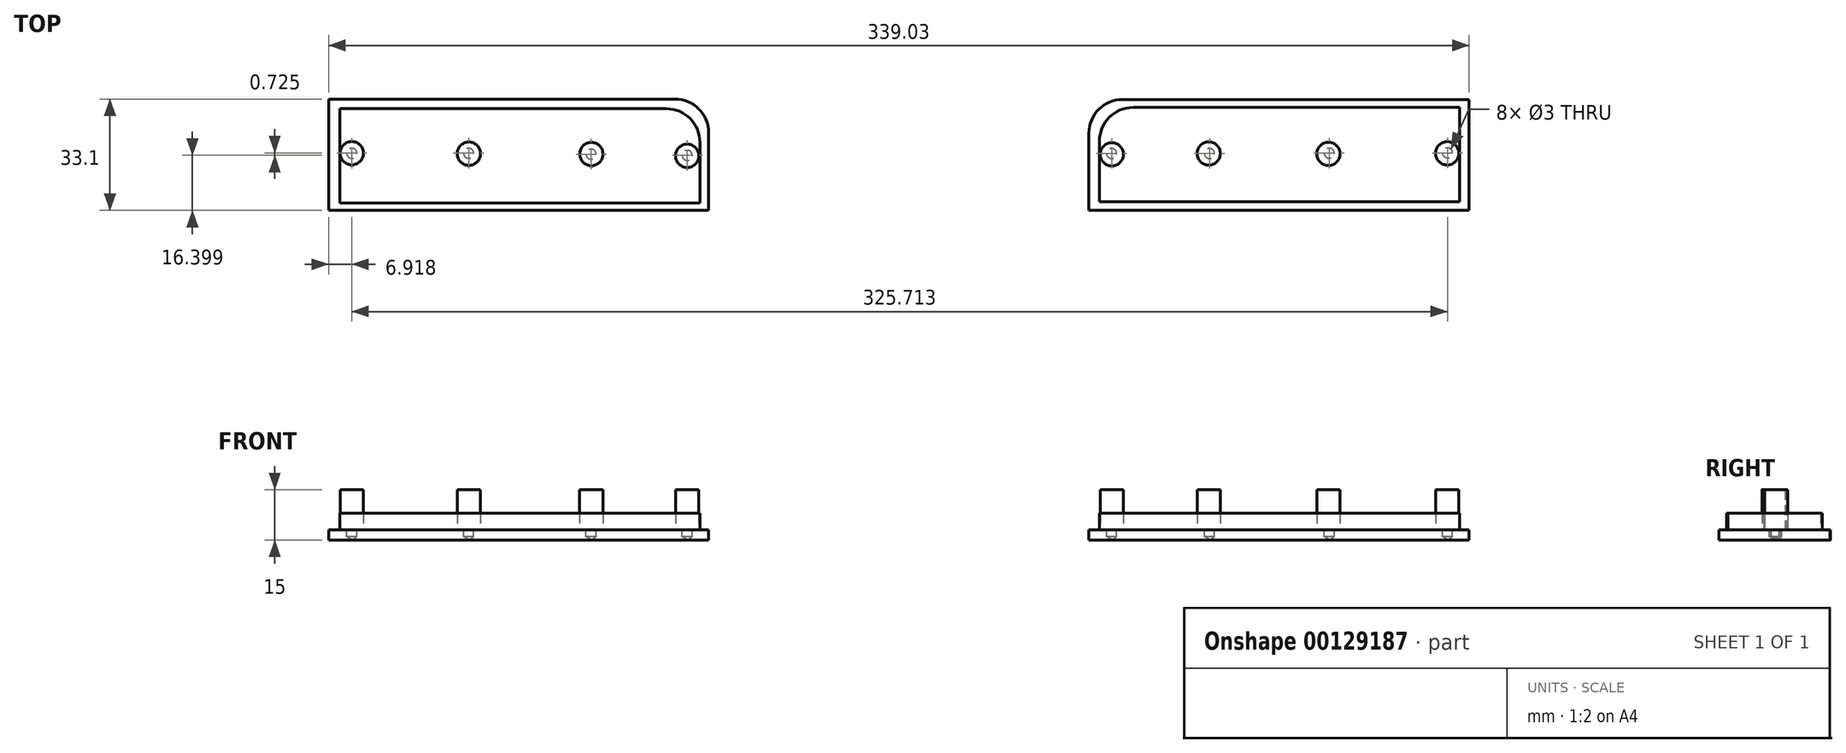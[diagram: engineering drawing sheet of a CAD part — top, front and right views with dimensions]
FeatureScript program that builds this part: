
annotation { "Feature Type Name" : "Feature", "Feature Type Description" : "" }
export const myFeature = defineFeature(function(context is Context, id is Id, definition is map)
    precondition{}
    {
        {
            var Q0;
            Q0=qCreatedBy(makeId("Top.planeOp"),FACE);
            var sketch = newSketch(context, id + "F0", { "sketchPlane" : qUnion([Q0])});
            skLineSegment(sketch, "E0.bottom", {"start": v(66.11, 78.9) * mm, "end": v(169.11, 78.9) * mm});
            skLineSegment(sketch, "E0.top", {"start": v(56.11, 45.9) * mm, "end": v(169.11, 45.9) * mm});
            skLineSegment(sketch, "E0.left", {"start": v(56.11, 68.9) * mm, "end": v(56.11, 45.9) * mm});
            skLineSegment(sketch, "E0.right", {"start": v(169.11, 78.9) * mm, "end": v(169.11, 45.9) * mm});
            skLineSegment(sketch, "E1.bottom", {"start": v(-169.92, 79) * mm, "end": v(-66.92, 79) * mm});
            skLineSegment(sketch, "E1.top", {"start": v(-169.92, 46) * mm, "end": v(-56.92, 46) * mm});
            skLineSegment(sketch, "E1.left", {"start": v(-169.92, 79) * mm, "end": v(-169.92, 46) * mm});
            skLineSegment(sketch, "E1.right", {"start": v(-56.92, 69) * mm, "end": v(-56.92, 46) * mm});
            skPoint(sketch, "E2.visualSharp", {"position": v(-56.92, 79) * mm});
            skArc(sketch, "E2.filletArc", {"start": v(-56.92, 69) * mm, "mid": v(-59.85, 76.07) * mm, "end": v(-66.92, 79) * mm});
            skPoint(sketch, "E3.visualSharp", {"position": v(56.11, 78.9) * mm});
            skArc(sketch, "E3.filletArc", {"start": v(66.11, 78.9) * mm, "mid": v(59.04, 75.97) * mm, "end": v(56.11, 68.9) * mm});
            skSolve(sketch);
        }
        {
            var Q0;
            Q0=qSketchRegion(id+"F0",true);
            extrude(context, id + "F1", {"entities" : qUnion([Q0]), "depth" : 3 * mm});
        }
        {
            var Q0;
            Q0=makeQuery(id+"F1.opExtrude","CAP_FACE",FACE,{"disambiguationData":[OSD([sQuery(id+"F0.wireOp",EDGE,"E0.bottom"),sQuery(id+"F0.wireOp",EDGE,"E0.top"),sQuery(id+"F0.wireOp",EDGE,"E0.left"),sQuery(id+"F0.wireOp",EDGE,"E0.right"),sQuery(id+"F0.wireOp",EDGE,"E3.filletArc")])],"isStart":false});
            cPlane(context, id + "F2", {"entities" : qUnion([Q0]), "cplaneType" : CPlaneType.OFFSET, "offset" : 25 * mm, "width" : 150 * mm, "height" : 150 * mm});
        }
        {
            var Q0;
            Q0=makeQuery(id+"F1.opExtrude","CAP_FACE",FACE,{"disambiguationData":[OSD([sQuery(id+"F0.wireOp",EDGE,"E1.bottom"),sQuery(id+"F0.wireOp",EDGE,"E1.top"),sQuery(id+"F0.wireOp",EDGE,"E1.left"),sQuery(id+"F0.wireOp",EDGE,"E1.right"),sQuery(id+"F0.wireOp",EDGE,"E2.filletArc")])],"isStart":false});
            cPlane(context, id + "F3", {"entities" : qUnion([Q0]), "cplaneType" : CPlaneType.OFFSET, "offset" : 0 * mm, "width" : 150 * mm, "height" : 150 * mm});
        }
        {
            var Q0;
            Q0=makeQuery(id+"F1.opExtrude","CAP_FACE",FACE,{"disambiguationData":[OSD([sQuery(id+"F0.wireOp",EDGE,"E1.bottom"),sQuery(id+"F0.wireOp",EDGE,"E1.top"),sQuery(id+"F0.wireOp",EDGE,"E1.left"),sQuery(id+"F0.wireOp",EDGE,"E1.right"),sQuery(id+"F0.wireOp",EDGE,"E2.filletArc")])],"isStart":false});
            cPlane(context, id + "F4", {"entities" : qUnion([Q0]), "cplaneType" : CPlaneType.OFFSET, "offset" : 0 * mm, "width" : 150 * mm, "height" : 150 * mm});
        }
        {
            var Q0;
            Q0=qCreatedBy(id+"F4.planeOp",FACE);
            var sketch = newSketch(context, id + "F5", { "sketchPlane" : qUnion([Q0])});
            skLineSegment(sketch, "E4.bottom", {"start": v(-166.51, 76.14) * mm, "end": v(-69.51, 76.14) * mm});
            skLineSegment(sketch, "E4.top", {"start": v(-166.51, 48.14) * mm, "end": v(-59.51, 48.14) * mm});
            skLineSegment(sketch, "E4.left", {"start": v(-166.51, 76.14) * mm, "end": v(-166.51, 48.14) * mm});
            skLineSegment(sketch, "E4.right", {"start": v(-59.51, 66.14) * mm, "end": v(-59.51, 48.14) * mm});
            skArc(sketch, "E5.filletArc", {"start": v(-59.51, 66.14) * mm, "mid": v(-62.44, 73.21) * mm, "end": v(-69.51, 76.14) * mm});
            skLineSegment(sketch, "E6.bottom", {"start": v(59.25, 48.54) * mm, "end": v(166.25, 48.54) * mm});
            skLineSegment(sketch, "E6.top", {"start": v(69.25, 76.54) * mm, "end": v(166.25, 76.54) * mm});
            skLineSegment(sketch, "E6.left", {"start": v(59.25, 48.54) * mm, "end": v(59.25, 66.54) * mm});
            skLineSegment(sketch, "E6.right", {"start": v(166.25, 48.54) * mm, "end": v(166.25, 76.54) * mm});
            skPoint(sketch, "E7.visualSharp", {"position": v(59.25, 76.54) * mm});
            skArc(sketch, "E7.filletArc", {"start": v(69.25, 76.54) * mm, "mid": v(62.18, 73.6) * mm, "end": v(59.25, 66.54) * mm});
            skSolve(sketch);
        }
        {
            var Q0;
            Q0 = qSketchRegion(id + "F5", true);
            extrude(context, id + "F6", {"entities" : qUnion([Q0]), "depth" : 5 * mm});
        }
        {
            var Q0;
            Q0=qCreatedBy(id+"F4.planeOp",FACE);
            var sketch = newSketch(context, id + "F7", { "sketchPlane" : qUnion([Q0])});
            skCircle(sketch, "E8", {"center": v(-163, 62.9) * mm, "radius": 3.46 * mm});
            skCircle(sketch, "E9", {"center": v(-128.2, 62.78) * mm, "radius": 3.46 * mm});
            skCircle(sketch, "E10", {"center": v(-91.8, 62.66) * mm, "radius": 3.46 * mm});
            skCircle(sketch, "E11", {"center": v(-63.32, 62.14) * mm, "radius": 3.46 * mm});
            skCircle(sketch, "E12", {"center": v(62.91, 62.57) * mm, "radius": 3.46 * mm});
            skCircle(sketch, "E13", {"center": v(91.73, 62.84) * mm, "radius": 3.46 * mm});
            skCircle(sketch, "E14", {"center": v(127.32, 62.72) * mm, "radius": 3.46 * mm});
            skCircle(sketch, "E15", {"center": v(162.64, 62.89) * mm, "radius": 3.46 * mm});
            skSolve(sketch);
        }
        {
            var Q0;
            Q0 = qSketchRegion(id + "F7", true);
            extrude(context, id + "F8", {"entities" : qUnion([Q0]), "depth" : 12 * mm});
        }
        {
            var Q0;
            Q0=makeQuery(id+"F8.opExtrude","CAP_FACE",FACE,{"disambiguationData":[OSD([sQuery(id+"F7.wireOp",EDGE,"E8")])],"isStart":false});
            var sketch = newSketch(context, id + "F9", { "sketchPlane" : qUnion([Q0])});
            skPoint(sketch, "E16", {"position": v(-163, 62.9) * mm});
            skPoint(sketch, "E17", {"position": v(-128.27, 62.9) * mm});
            skPoint(sketch, "E18", {"position": v(-91.88, 62.65) * mm});
            skPoint(sketch, "E19", {"position": v(-63.3, 62.3) * mm});
            skPoint(sketch, "E20", {"position": v(62.87, 62.84) * mm});
            skPoint(sketch, "E21", {"position": v(91.95, 62.84) * mm});
            skPoint(sketch, "E22", {"position": v(127.56, 62.93) * mm});
            skPoint(sketch, "E23", {"position": v(162.71, 63.02) * mm});
            skSolve(sketch);
        }
        {
            var Q0;
            Q0=sQuery(id+"F9.wireOp",VERTEX,"E16");
            var Q1;
            Q1=sQuery(id+"F9.wireOp",VERTEX,"E17");
            var Q2;
            Q2=sQuery(id+"F9.wireOp",VERTEX,"E18");
            var Q3;
            Q3=sQuery(id+"F9.wireOp",VERTEX,"E19");
            var Q4;
            Q4=sQuery(id+"F9.wireOp",VERTEX,"E20");
            var Q5;
            Q5=sQuery(id+"F9.wireOp",VERTEX,"E21");
            var Q6;
            Q6=sQuery(id+"F9.wireOp",VERTEX,"E22");
            var Q7;
            Q7=sQuery(id+"F9.wireOp",VERTEX,"E23");
            var Q8;
            Q8=makeQuery(id+"F1.opExtrude","SWEPT_BODY",BODY,{"disambiguationData":[OSD([sQuery(id+"F0.wireOp",EDGE,"E1.bottom"),sQuery(id+"F0.wireOp",EDGE,"E1.top"),sQuery(id+"F0.wireOp",EDGE,"E1.left"),sQuery(id+"F0.wireOp",EDGE,"E1.right"),sQuery(id+"F0.wireOp",EDGE,"E2.filletArc")])]});
            var Q9;
            Q9=makeQuery(id+"F1.opExtrude","SWEPT_BODY",BODY,{"disambiguationData":[OSD([sQuery(id+"F0.wireOp",EDGE,"E0.bottom"),sQuery(id+"F0.wireOp",EDGE,"E0.top"),sQuery(id+"F0.wireOp",EDGE,"E0.left"),sQuery(id+"F0.wireOp",EDGE,"E0.right"),sQuery(id+"F0.wireOp",EDGE,"E3.filletArc")])]});
            hole(context, id + "F10", {"style" : HoleStyle.SIMPLE, "endStyle" : HoleEndStyle.BLIND, "holeDiameter" : 3 * mm, "holeDepth" : 2 * mm, "locations" : qUnion([Q0, Q1, Q2, Q3, Q4, Q5, Q6, Q7]), "scope" : qUnion([Q8, Q9])});
        }
    });
